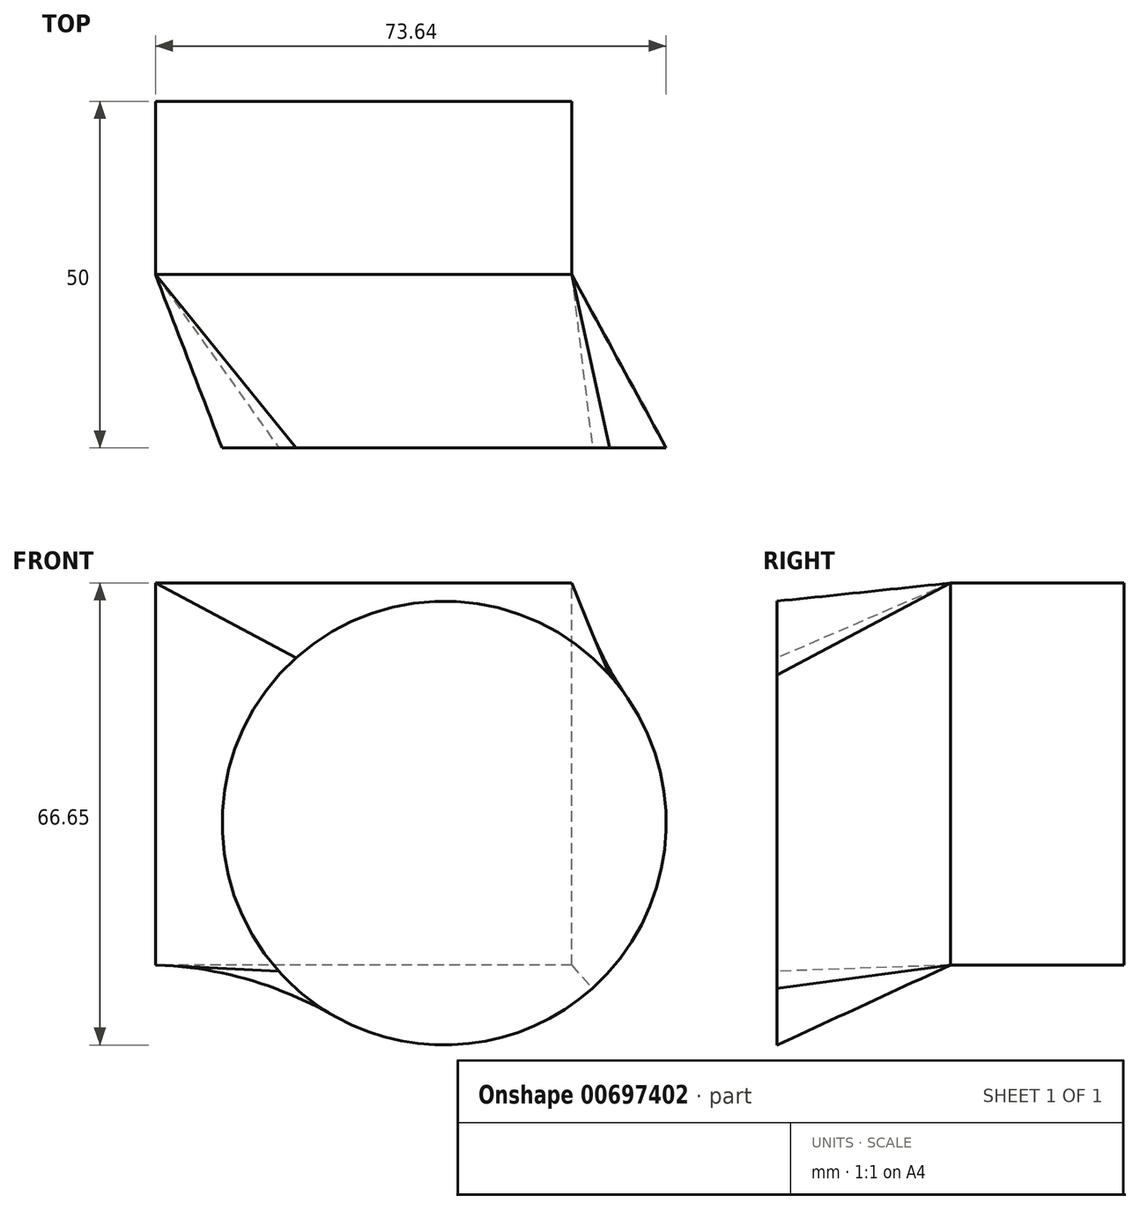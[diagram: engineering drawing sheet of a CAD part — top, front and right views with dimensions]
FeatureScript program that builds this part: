
annotation { "Feature Type Name" : "Feature", "Feature Type Description" : "" }
export const myFeature = defineFeature(function(context is Context, id is Id, definition is map)
    precondition{}
    {
        {
            var Q0;
            Q0=qCreatedBy(makeId("Front.planeOp"),FACE);
            var sketch = newSketch(context, id + "F0", { "sketchPlane" : qUnion([Q0])});
            skLineSegment(sketch, "E0.bottom", {"start": v(30, -27.56) * mm, "end": v(-30, -27.56) * mm});
            skLineSegment(sketch, "E0.top", {"start": v(30, 27.56) * mm, "end": v(-30, 27.56) * mm});
            skLineSegment(sketch, "E0.left", {"start": v(30, -27.56) * mm, "end": v(30, 27.56) * mm});
            skLineSegment(sketch, "E0.right", {"start": v(-30, -27.56) * mm, "end": v(-30, 27.56) * mm});
            skPoint(sketch, "E0.middle", {"position": v(0, 0) * mm});
            skSolve(sketch);
        }
        {
            var Q0;
            Q0=makeQuery(id+"F0.imprint","IMPRINT",FACE,{"disambiguationData":[TD([[makeQuery(id+"F0.imprint","IMPRINT",EDGE,{"derivedFrom":sQuery(id+"F0.wireOp",EDGE,"E0.bottom")}),-1.0]])]});
            extrude(context, id + "F1", {"entities" : qUnion([Q0]), "depth" : 25 * mm, "offsetDistance" : 25 * mm});
        }
        {
            var Q0;
            Q0=qCreatedBy(makeId("Front.planeOp"),FACE);
            cPlane(context, id + "F2", {"entities" : qUnion([Q0]), "cplaneType" : CPlaneType.OFFSET, "offset" : 50 * mm, "width" : 150 * mm, "height" : 150 * mm});
        }
        {
            var Q0;
            Q0=qCreatedBy(id+"F2.planeOp",FACE);
            var sketch = newSketch(context, id + "F3", { "sketchPlane" : qUnion([Q0])});
            skCircle(sketch, "E1", {"center": v(11.63, -7.08) * mm, "radius": 32.02 * mm});
            skSolve(sketch);
        }
        {
            var Q0;
            Q0=makeQuery(id+"F1.opExtrude","CAP_FACE",FACE,{"disambiguationData":[OSD([sQuery(id+"F0.wireOp",EDGE,"E0.bottom"),sQuery(id+"F0.wireOp",EDGE,"E0.top"),sQuery(id+"F0.wireOp",EDGE,"E0.left"),sQuery(id+"F0.wireOp",EDGE,"E0.right")])],"isStart":false});
            var Q1;
            Q1=makeQuery(id+"F3.imprint","IMPRINT",FACE,{"disambiguationData":[TD([[makeQuery(id+"F3.imprint","IMPRINT",EDGE,{"derivedFrom":sQuery(id+"F3.wireOp",EDGE,"E1")}),1.0]])]});
            loft(context, id + "F4", {"sheetProfilesArray" : [{ "sheetProfileEntities" : qUnion([Q0]) }, { "sheetProfileEntities" : qUnion([Q1]) }]});
        }
    });
